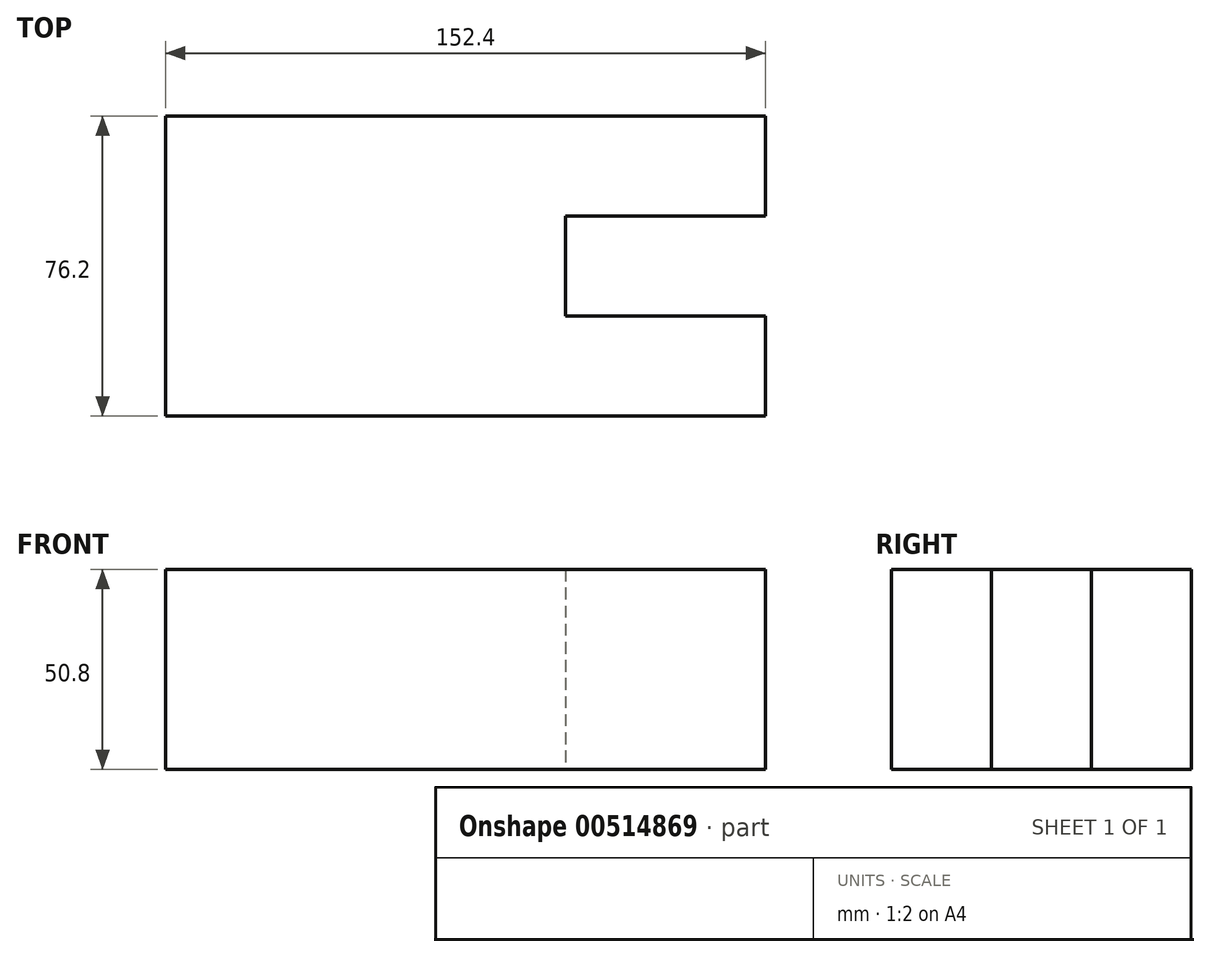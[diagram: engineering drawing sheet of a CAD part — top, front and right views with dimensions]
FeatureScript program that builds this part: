
annotation { "Feature Type Name" : "Feature", "Feature Type Description" : "" }
export const myFeature = defineFeature(function(context is Context, id is Id, definition is map)
    precondition{}
    {
        {
            var Q0;
            Q0=qCreatedBy(makeId("Top.planeOp"),FACE);
            var sketch = newSketch(context, id + "F0", { "sketchPlane" : qUnion([Q0])});
            skLineSegment(sketch, "E0", {"start": v(-82.95, 61.5) * mm, "end": v(69.45, 61.5) * mm});
            skLineSegment(sketch, "E1", {"start": v(69.45, 61.5) * mm, "end": v(69.45, 36.1) * mm});
            skLineSegment(sketch, "E2", {"start": v(69.45, 36.1) * mm, "end": v(18.65, 36.1) * mm});
            skLineSegment(sketch, "E3", {"start": v(18.65, 36.1) * mm, "end": v(18.65, 10.7) * mm});
            skLineSegment(sketch, "E4", {"start": v(18.65, 10.7) * mm, "end": v(69.45, 10.7) * mm});
            skLineSegment(sketch, "E5", {"start": v(69.45, 10.7) * mm, "end": v(69.45, -14.7) * mm});
            skLineSegment(sketch, "E6", {"start": v(69.45, -14.7) * mm, "end": v(-82.95, -14.7) * mm});
            skLineSegment(sketch, "E7", {"start": v(-82.95, -14.7) * mm, "end": v(-82.95, 61.5) * mm});
            skSolve(sketch);
        }
        {
            var Q0;
            Q0 = qSketchRegion(id + "F0", true);
            extrude(context, id + "F1", {"entities" : qUnion([Q0]), "depth" : 50.8 * mm, "offsetDistance" : 25.4 * mm});
        }
    });
